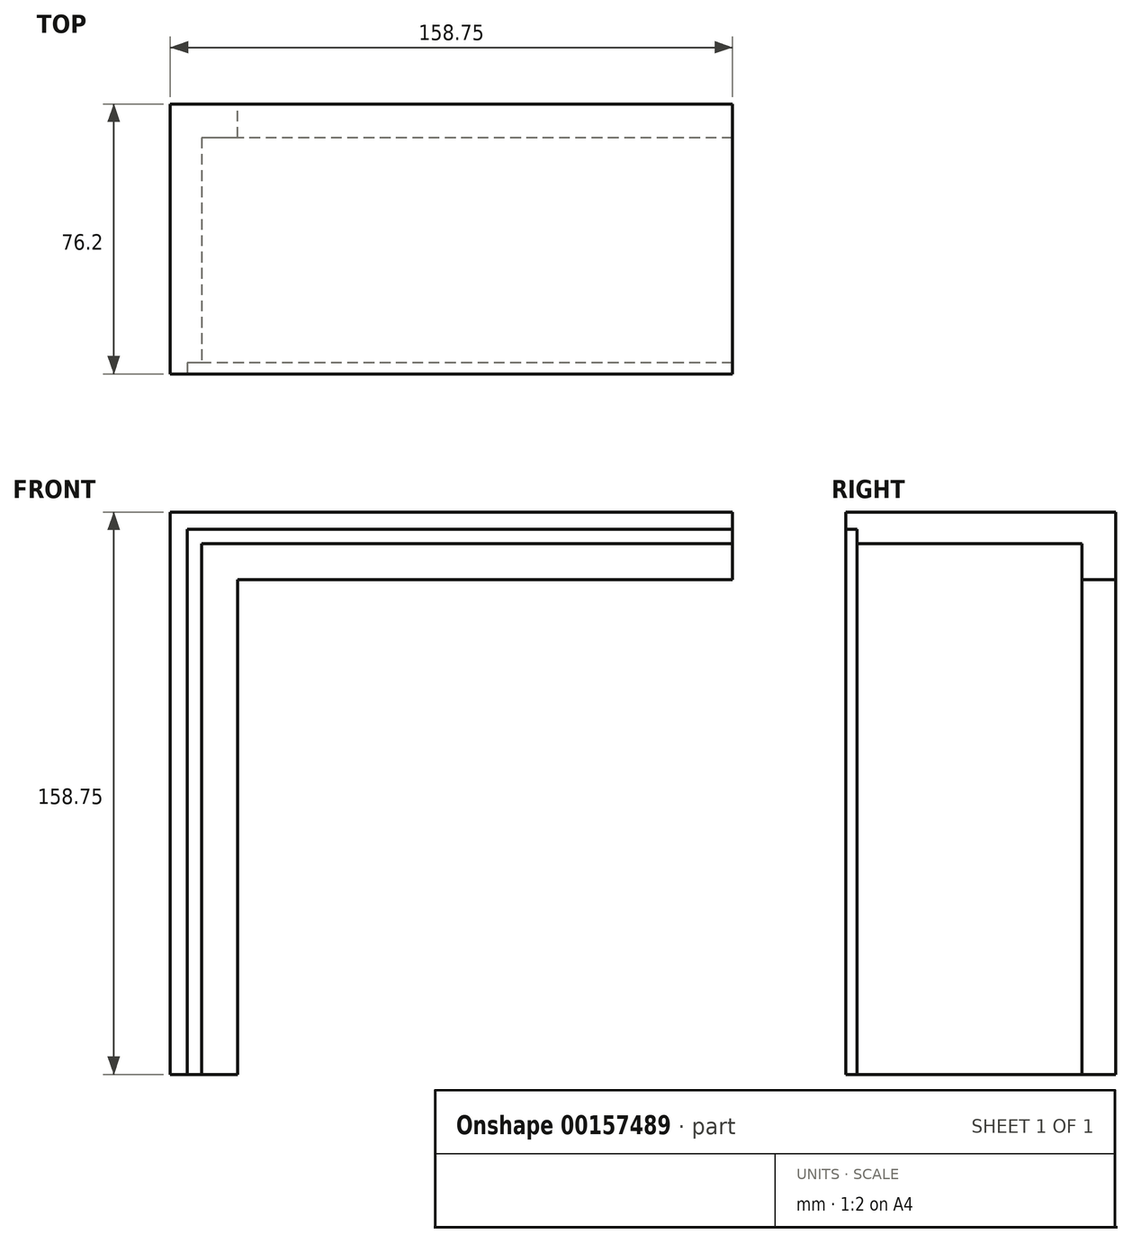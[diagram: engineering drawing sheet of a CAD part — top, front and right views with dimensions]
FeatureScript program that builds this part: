
annotation { "Feature Type Name" : "Feature", "Feature Type Description" : "" }
export const myFeature = defineFeature(function(context is Context, id is Id, definition is map)
    precondition{}
    {
        {
            var Q0;
            Q0=qCreatedBy(makeId("Front.planeOp"),FACE);
            var sketch = newSketch(context, id + "F0", { "sketchPlane" : qUnion([Q0])});
            skLineSegment(sketch, "E0", {"start": v(0, 180.55) * mm, "end": v(0, -185.02) * mm, "construction": true});
            skLineSegment(sketch, "E1", {"start": v(-187.82, 0) * mm, "end": v(184.46, 0) * mm, "construction": true});
            skLineSegment(sketch, "E2", {"start": v(0, 158.75) * mm, "end": v(-158.75, 158.75) * mm});
            skLineSegment(sketch, "E3", {"start": v(-158.75, 158.75) * mm, "end": v(-158.75, 0) * mm});
            skLineSegment(sketch, "E4", {"start": v(0, 139.7) * mm, "end": v(-139.7, 139.7) * mm});
            skLineSegment(sketch, "E5", {"start": v(-139.7, 139.7) * mm, "end": v(-139.7, 0) * mm});
            skLineSegment(sketch, "E6", {"start": v(-158.75, 0) * mm, "end": v(-139.7, 0) * mm});
            skLineSegment(sketch, "E7", {"start": v(0, 158.75) * mm, "end": v(0, 139.7) * mm});
            skSolve(sketch);
        }
        {
            var Q0;
            Q0 = qSketchRegion(id + "F0", true);
            var Q1;
            Q1 = qSketchRegion(id + "F2", true);
            extrude(context, id + "F1", {"entities" : qUnion([Q0, Q1]), "depth" : 76.2 * mm});
        }
        {
            var Q0;
            Q0=makeQuery(id+"F1.opExtrude","CAP_FACE",FACE,{"disambiguationData":[OSD([sQuery(id+"F0.wireOp",EDGE,"E2"),sQuery(id+"F0.wireOp",EDGE,"E3"),sQuery(id+"F0.wireOp",EDGE,"E4"),sQuery(id+"F0.wireOp",EDGE,"E5"),sQuery(id+"F0.wireOp",EDGE,"E6"),sQuery(id+"F0.wireOp",EDGE,"E7")])],"isStart":false});
            var sketch = newSketch(context, id + "F2", { "sketchPlane" : qUnion([Q0])});
            skLineSegment(sketch, "E8", {"start": v(0, -83.24) * mm, "end": v(0, 158.75) * mm, "construction": true});
            skLineSegment(sketch, "E9", {"start": v(-158.75, 0) * mm, "end": v(101.88, 0) * mm, "construction": true});
            skLineSegment(sketch, "E10.bottom", {"start": v(0, 0) * mm, "end": v(-153.92, 0) * mm});
            skLineSegment(sketch, "E10.top", {"start": v(0, 153.92) * mm, "end": v(-153.92, 153.92) * mm});
            skLineSegment(sketch, "E10.left", {"start": v(0, 0) * mm, "end": v(0, 153.92) * mm});
            skLineSegment(sketch, "E10.right", {"start": v(-153.92, 0) * mm, "end": v(-153.92, 153.92) * mm});
            skSolve(sketch);
        }
        {
            var Q0;
            Q0 = qSketchRegion(id + "F2", true);
            extrude(context, id + "F3", {"entities" : qUnion([Q0]), "operationType" : NewBodyOperationType.REMOVE, "oppositeDirection" : true, "depth" : 3.17 * mm});
        }
        {
            var Q0;
            Q0=makeQuery(id+"F3.boolean.opBoolean","COPY",FACE,{"derivedFrom":makeQuery(id+"F3.opExtrude","CAP_FACE",FACE,{"disambiguationData":[OSD([sQuery(id+"F2.wireOp",EDGE,"E10.bottom"),sQuery(id+"F2.wireOp",EDGE,"E10.top"),sQuery(id+"F2.wireOp",EDGE,"E10.left"),sQuery(id+"F2.wireOp",EDGE,"E10.right")])],"isStart":false})});
            var sketch = newSketch(context, id + "F4", { "sketchPlane" : qUnion([Q0])});
            skLineSegment(sketch, "E11", {"start": v(0, 160.99) * mm, "end": v(0, -63.1) * mm, "construction": true});
            skLineSegment(sketch, "E12", {"start": v(-161.28, 0) * mm, "end": v(50.92, 0) * mm, "construction": true});
            skLineSegment(sketch, "E13.bottom", {"start": v(0, 0) * mm, "end": v(-149.86, 0) * mm});
            skLineSegment(sketch, "E13.top", {"start": v(0, 149.86) * mm, "end": v(-149.86, 149.86) * mm});
            skLineSegment(sketch, "E13.left", {"start": v(0, 0) * mm, "end": v(0, 149.86) * mm});
            skLineSegment(sketch, "E13.right", {"start": v(-149.86, 0) * mm, "end": v(-149.86, 149.86) * mm});
            skSolve(sketch);
        }
        {
            var Q0;
            Q0 = qSketchRegion(id + "F4", true);
            extrude(context, id + "F5", {"entities" : qUnion([Q0]), "operationType" : NewBodyOperationType.REMOVE, "oppositeDirection" : true, "depth" : 63.5 * mm});
        }
    });
